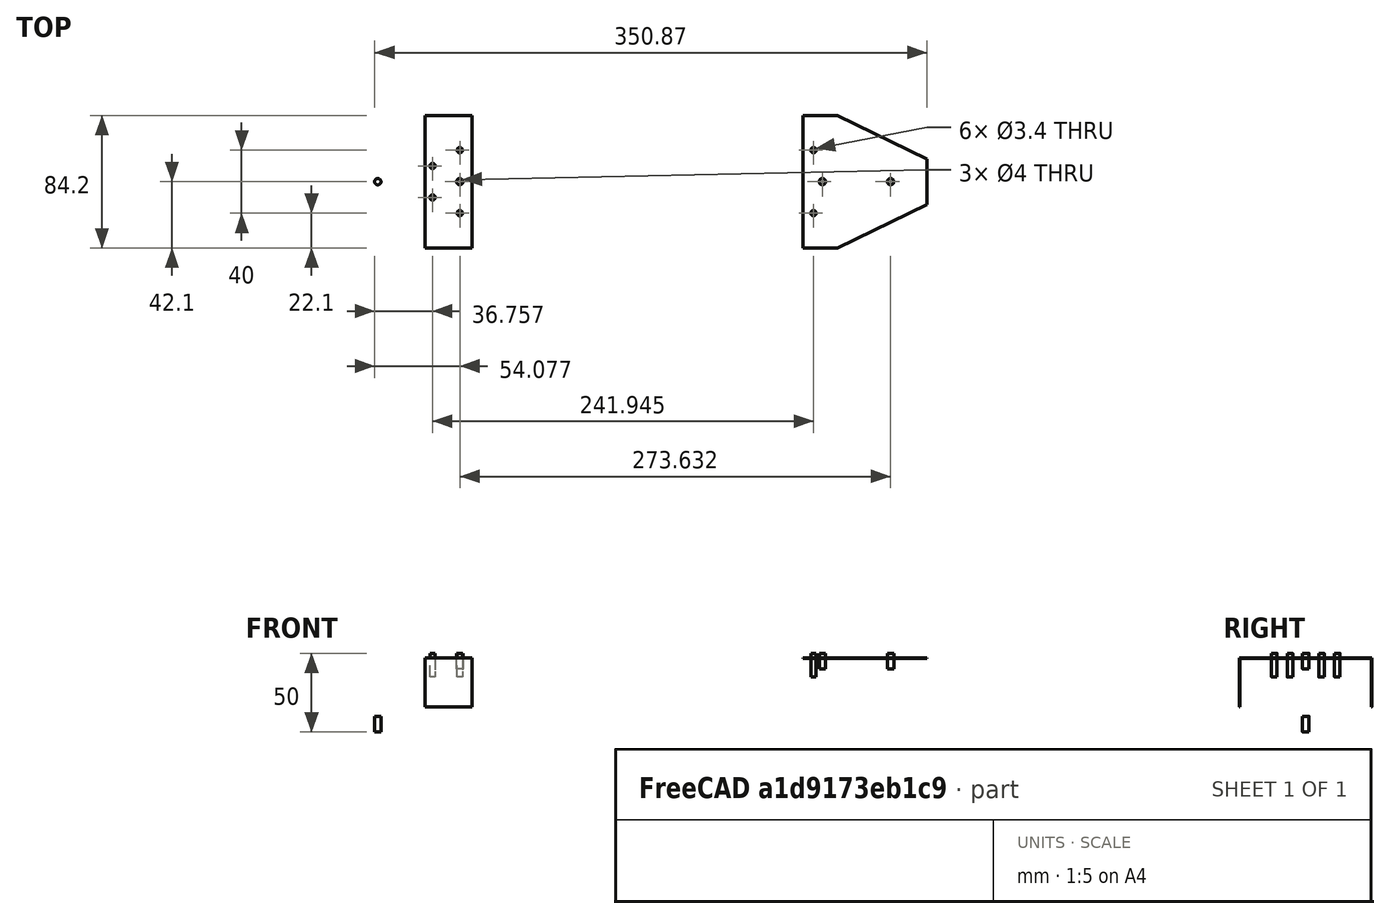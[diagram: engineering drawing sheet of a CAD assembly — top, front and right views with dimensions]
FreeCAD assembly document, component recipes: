
FREECAD ASSEMBLY — COMPONENT RECIPES ("composit_stand3_dropper_fix_cap_inner_model")

This assembly document has 3 components, labeled P0..P2 below (a component is one placed body or linked part). 3 of them carry a construction recipe — the FreeCAD feature program that regenerates the part from scratch, quoted from this document or its linked companion documents; the rest are supplied as boundary geometry only. No exploded tour is included for this assembly.
COMPONENT P0 — recipe-attached ("cap_inner_1", modeled in this document).
Construction recipe (the document's own serialized feature program — sketch geometry with constraints, then the solid features built on it; lengths are millimeters unless a unit is written):

FEATURE [PartDesign::SubShapeBinder] Binder
  BindCopyOnChange = 0
  BindMode = 0
  ClaimChildren = true
  Context = -> Body [Binder.]
  Fuse = false
  MakeFace = true
  OffsetFill = false
  OffsetIntersection = false
  OffsetJoinType = 0
  OffsetOpenResult = false
  PartialLoad = false
  Placement = pos=(30,0,0) rot=(0,-1,0;1.5708rad)
  Relative = true
  Support = -> [Sketch]
  _Version = 2
FEATURE [PartDesign::FeaturePython] BaseBend  # WARN: FeaturePython — macro-defined, semantics opaque (R4)
  BendSide = 1
  BendSketch = -> Binder
  MidPlane = false
  Reverse = true
  Suppressed = false
  length = 30
  radius = 0.1
  thickness = 0.3
FEATURE [PartDesign::Boolean] Boolean
  BaseFeature = -> BaseBend
  Group = -> [Fusion]
  Suppressed = false
  Type = 1
  UsePlacement = true
FEATURE [PartDesign::CoordinateSystem] Local_CS
  AttacherType = Attacher::AttachEngine3D
  AttachmentSupport = -> [XY_Plane]
  MapMode = 5
FEATURE [PartDesign::Body] Body  label="cap_inner_1"
  AllowCompound = false
  Group = -> [Binder,BaseBend,Boolean,Local_CS]
  Origin = -> Origin
  Tip = -> Boolean
COMPONENT P1 — recipe-attached ("cap_inner_2", modeled in this document).
Construction recipe (the document's own serialized feature program — sketch geometry with constraints, then the solid features built on it; lengths are millimeters unless a unit is written):

FEATURE [PartDesign::SubShapeBinder] Binder001
  BindCopyOnChange = 0
  BindMode = 0
  ClaimChildren = false
  Context = -> Body001 [Binder001.]
  Fuse = false
  MakeFace = true
  OffsetFill = false
  OffsetIntersection = false
  OffsetJoinType = 0
  OffsetOpenResult = false
  PartialLoad = false
  Placement = pos=(0,0,37) rot=(0,0,1;0rad)
  Relative = true
  Support = -> [Connect]
  _Version = 2
  expr: .Placement.Base.z = <<composit_stand3_dropper_fix_cap_outer_main>>#<<Properties>>.height - 3 mm
  expr: Support = <<Connect>>._self
FEATURE [PartDesign::FeaturePython] BaseBend001  # WARN: FeaturePython — macro-defined, semantics opaque (R4)
  BendSide = 0
  BendSketch = -> Binder001
  MidPlane = false
  Reverse = true
  Suppressed = false
  length = 70
  radius = 0.1
  thickness = 0.3
FEATURE [PartDesign::Boolean] Boolean001
  BaseFeature = -> BaseBend001
  Group = -> [Fusion001]
  Suppressed = false
  Type = 1
  UsePlacement = true
FEATURE [PartDesign::CoordinateSystem] Local_CS001
  AttacherType = Attacher::AttachEngine3D
  AttachmentSupport = -> [XY_Plane001]
  MapMode = 5
FEATURE [PartDesign::Body] Body001  label="cap_inner_2"
  AllowCompound = false
  Group = -> [Binder001,BaseBend001,Boolean001,Local_CS001]
  Origin = -> Origin001
  Tip = -> Boolean001
COMPONENT P2 — recipe-attached ("hole_3.4mm_rev", a linked part whose construction recipe lives in a companion FreeCAD document of the same project; that document's serialized recipe follows).
Construction recipe (the companion document, serialized — sketch geometry with constraints, then the solid features built on it; lengths are millimeters unless a unit is written):

FCSTD DOCUMENT  (FreeCAD 1.1R38827 (Git))
Label: composit_stand3_main
License: All rights reserved
LicenseURL: http://en.wikipedia.org/wiki/All_rights_reserved
objects: Part::Cylinder×2, Sketcher::SketchObject×1, Part::FeaturePython×1
note: 5 computed .brp shape members not serialized (recipe doc carries the construction recipe); baked Part::Feature solids carry a one-line shape summary decoded from their .brp

FEATURE [Sketcher::SketchObject] Sketch  label="main_sketch"
  ArcFitTolerance = 0
  FullyConstrained = true
  MakeInternals = false
  sketch-geometry (4):
    g0: LineSegment [constr] StartX=0 StartY=0 StartZ=0 EndX=8.37158 EndY=14.5 EndZ=0
    g1: LineSegment StartX=8.37158 StartY=14.5 StartZ=0 EndX=351.872 EndY=14.5 EndZ=0
    g2: LineSegment StartX=351.872 StartY=14.5 StartZ=0 EndX=351.872 EndY=0 EndZ=0
    g3: GeomPoint [constr] X=351.872 Y=-14.5 Z=0
  constraints (13):
    c: Coincident(g-1,g0)
    c: Horizontal(g1)
    c: Coincident(g1,g2)
    c: PointOnObject(g2,g-1)
    c: Vertical(g2)
    c: Angle(g0) = 1.0472
    c: DistanceX(g0,g1) = 343.5  'face_width'
    c: DistanceY(g3,g1) = 29  'end_width'
    c: Symmetric(g3,g1,g2)
    c: DistanceX(g0) = 8.37158  'x_face_offset'
    c: Coincident(g1,g0)
    c: Distance(g0) = 16.7432  'corner_distance'
    c: DistanceY(g0,g0) = 14.5
FEATURE [Part::FeaturePython] LinearArray  label="modules_placement_x"  # WARN: FeaturePython — macro-defined, semantics opaque (R4)
  Alignment = 0
  CellStart = A1
  Count = 2
  Dir = (1,0,0)
  DirIsDriven = true
  DistributionLaw = 0
  DrivenProperty = 1
  EndInclusive = true
  ExposePlacement = false
  GeneratorMode = 0
  MarkerShape = 1
  MarkerSize = 0
  NumElements = 2
  OrientMode = 1
  Placement = pos=(8.37158,14.5,0) rot=(0,0,1;0rad)
  Point = (0,0,0)
  PointIsDriven = true
  Reverse = false
  SpanEnd = 248
  SpanStart = 98
  Step = 150
  Type = lattice2LinearArray.LinearArray
  VSGVersion = 1
  Values = 98.0 | 248.0
  ValuesSource = 2
  isLattice = 1
  expr: .Placement.Base.x = <<main_sketch>>.Constraints.end_width / 2 / tan(60)
  expr: .Placement.Base.y = <<main_sketch>>.Constraints.end_width / 2
FEATURE [Part::Cylinder] Cylinder  label="hole_3.4mm"
  Angle = 360
  AttacherType = Attacher::AttachEngine3D
  FirstAngle = 0
  Height = 15
  Radius = 1.7
  SecondAngle = 0
FEATURE [Part::Cylinder] Cylinder001  label="hole_3.4mm_rev"
  Angle = 360
  AttacherType = Attacher::AttachEngine3D
  FirstAngle = 0
  Height = 15
  Placement = pos=(0,0,0) rot=(1,0,0;3.14159rad)
  Radius = 1.7
  SecondAngle = 0
PROVENANCE & LICENSES
A FreeCAD (.FCStd) document from a public repository crawl; recipes are the document's own serialized feature recipes (and, for linked parts, companion documents' recipes).
License: as declared in the source repository (recorded in the dataset sidecar).
